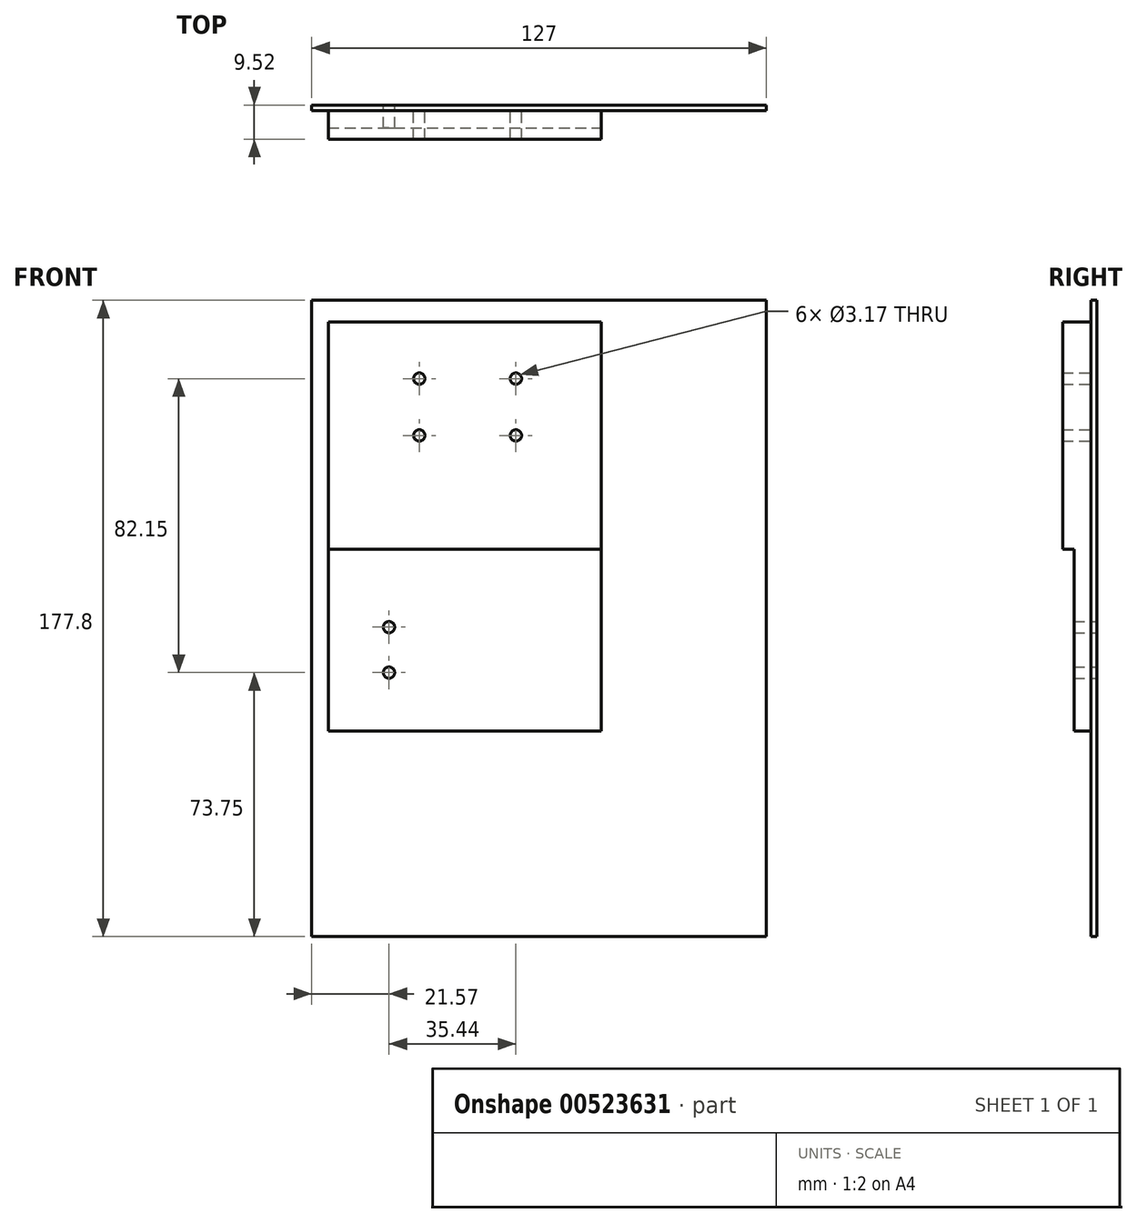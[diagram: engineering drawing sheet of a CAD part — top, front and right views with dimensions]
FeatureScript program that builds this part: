
annotation { "Feature Type Name" : "Feature", "Feature Type Description" : "" }
export const myFeature = defineFeature(function(context is Context, id is Id, definition is map)
    precondition{}
    {
        {
            var Q0;
            Q0=qCreatedBy(makeId("Front.planeOp"),FACE);
            var sketch = newSketch(context, id + "F0", { "sketchPlane" : qUnion([Q0])});
            skLineSegment(sketch, "E0.bottom", {"start": v(-101.45, 128.75) * mm, "end": v(25.55, 128.75) * mm});
            skLineSegment(sketch, "E0.top", {"start": v(-101.45, -49.05) * mm, "end": v(25.55, -49.05) * mm});
            skLineSegment(sketch, "E0.left", {"start": v(-101.45, 128.75) * mm, "end": v(-101.45, -49.05) * mm});
            skLineSegment(sketch, "E0.right", {"start": v(25.55, 128.75) * mm, "end": v(25.55, -49.05) * mm});
            skLineSegment(sketch, "E1.bottom", {"start": v(-96.82, 122.72) * mm, "end": v(-20.62, 122.72) * mm});
            skLineSegment(sketch, "E1.top", {"start": v(-96.82, 59.22) * mm, "end": v(-20.62, 59.22) * mm});
            skLineSegment(sketch, "E1.left", {"start": v(-96.82, 122.72) * mm, "end": v(-96.82, 59.22) * mm});
            skLineSegment(sketch, "E1.right", {"start": v(-20.62, 122.72) * mm, "end": v(-20.62, 59.22) * mm});
            skLineSegment(sketch, "E2.bottom", {"start": v(-85.71, 43.15) * mm, "end": v(-31.74, 43.15) * mm});
            skLineSegment(sketch, "E2.top", {"start": v(-85.71, 17.75) * mm, "end": v(-31.74, 17.75) * mm});
            skLineSegment(sketch, "E2.left", {"start": v(-85.71, 43.15) * mm, "end": v(-85.71, 17.75) * mm});
            skLineSegment(sketch, "E2.right", {"start": v(-31.74, 43.15) * mm, "end": v(-31.74, 17.75) * mm});
            skPoint(sketch, "E3", {"position": v(-71.42, 106.85) * mm});
            skPoint(sketch, "E4", {"position": v(-44.44, 106.85) * mm});
            skPoint(sketch, "E5", {"position": v(-44.44, 90.97) * mm});
            skPoint(sketch, "E6", {"position": v(-71.42, 90.97) * mm});
            skLineSegment(sketch, "E7", {"start": v(-58.72, 59.22) * mm, "end": v(-58.72, 43.15) * mm});
            skPoint(sketch, "E8", {"position": v(-79.88, 37.4) * mm});
            skPoint(sketch, "E9", {"position": v(-79.88, 24.7) * mm});
            skLineSegment(sketch, "E10.top", {"start": v(-96.82, 8.42) * mm, "end": v(-20.62, 8.42) * mm});
            skLineSegment(sketch, "E10.left", {"start": v(-96.82, 122.72) * mm, "end": v(-96.82, 8.42) * mm});
            skLineSegment(sketch, "E10.right", {"start": v(-20.62, 122.72) * mm, "end": v(-20.62, 8.42) * mm});
            skSolve(sketch);
        }
        {
            var Q0;
            Q0=makeQuery(id+"F0.imprint","IMPRINT",FACE,{"disambiguationData":[TD([[makeQuery(id+"F0.imprint","IMPRINT",EDGE,{"derivedFrom":sQuery(id+"F0.wireOp",EDGE,"E0.bottom")}),-1.0]])]});
            extrude(context, id + "F1", {"entities" : qUnion([Q0]), "depth" : 1.59 * mm, "offsetDistance" : 25.4 * mm});
        }
        {
            var Q0;
            {var subQ3=sQuery(id+"F0.wireOp",EDGE,"E1.bottom");Q0=makeQuery(id+"F0.imprint","IMPRINT",FACE,{"disambiguationData":[TD([[makeQuery(id+"F0.imprint","IMPRINT",EDGE,{"derivedFrom":subQ3}),-1.0]])]});}
            extrude(context, id + "F2", {"entities" : qUnion([Q0]), "operationType" : NewBodyOperationType.ADD, "depth" : 9.52 * mm, "offsetDistance" : 25.4 * mm});
        }
        {
            var Q0;
            Q0=makeQuery(id+"F0.imprint","IMPRINT",FACE,{"disambiguationData":[TD([[makeQuery(id+"F0.imprint","IMPRINT",EDGE,{"derivedFrom":sQuery(id+"F0.wireOp",EDGE,"E2.top")}),-1.0]])]});
            var Q1;
            Q1=makeQuery(id+"F0.imprint","IMPRINT",FACE,{"disambiguationData":[TD([[makeQuery(id+"F0.imprint","IMPRINT",EDGE,{"derivedFrom":sQuery(id+"F0.wireOp",EDGE,"E2.top")}),1.0]])]});
            extrude(context, id + "F3", {"entities" : qUnion([Q0, Q1]), "operationType" : NewBodyOperationType.ADD, "depth" : 6.35 * mm, "offsetDistance" : 25.4 * mm});
        }
        {
            var Q0;
            Q0=sQuery(id+"F0.wireOp",VERTEX,"E3");
            var Q1;
            Q1=sQuery(id+"F0.wireOp",VERTEX,"E4");
            var Q2;
            Q2=sQuery(id+"F0.wireOp",VERTEX,"E5");
            var Q3;
            Q3=sQuery(id+"F0.wireOp",VERTEX,"E6");
            var Q4;
            Q4=sQuery(id+"F0.wireOp",VERTEX,"E8");
            var Q5;
            Q5=sQuery(id+"F0.wireOp",VERTEX,"E9");
            var Q6;
            Q6=makeQuery(id+"F1.opExtrude","SWEPT_BODY",BODY,{"disambiguationData":[OSD([sQuery(id+"F0.wireOp",EDGE,"E0.bottom"),sQuery(id+"F0.wireOp",EDGE,"E0.top"),sQuery(id+"F0.wireOp",EDGE,"E0.left"),sQuery(id+"F0.wireOp",EDGE,"E0.right"),sQuery(id+"F0.wireOp",EDGE,"E1.bottom"),sQuery(id+"F0.wireOp",EDGE,"E10.top"),sQuery(id+"F0.wireOp",EDGE,"E10.left"),sQuery(id+"F0.wireOp",EDGE,"E10.right")])]});
            hole(context, id + "F4", {"style" : HoleStyle.SIMPLE, "endStyle" : HoleEndStyle.THROUGH, "oppositeDirection" : true, "holeDiameter" : 3.17 * mm, "isTappedThrough" : true, "tappedDepth" : 12.7 * mm, "tapClearance" : 3, "startFromSketch" : true, "locations" : qUnion([Q0, Q1, Q2, Q3, Q4, Q5]), "scope" : qUnion([Q6])});
        }
    });
